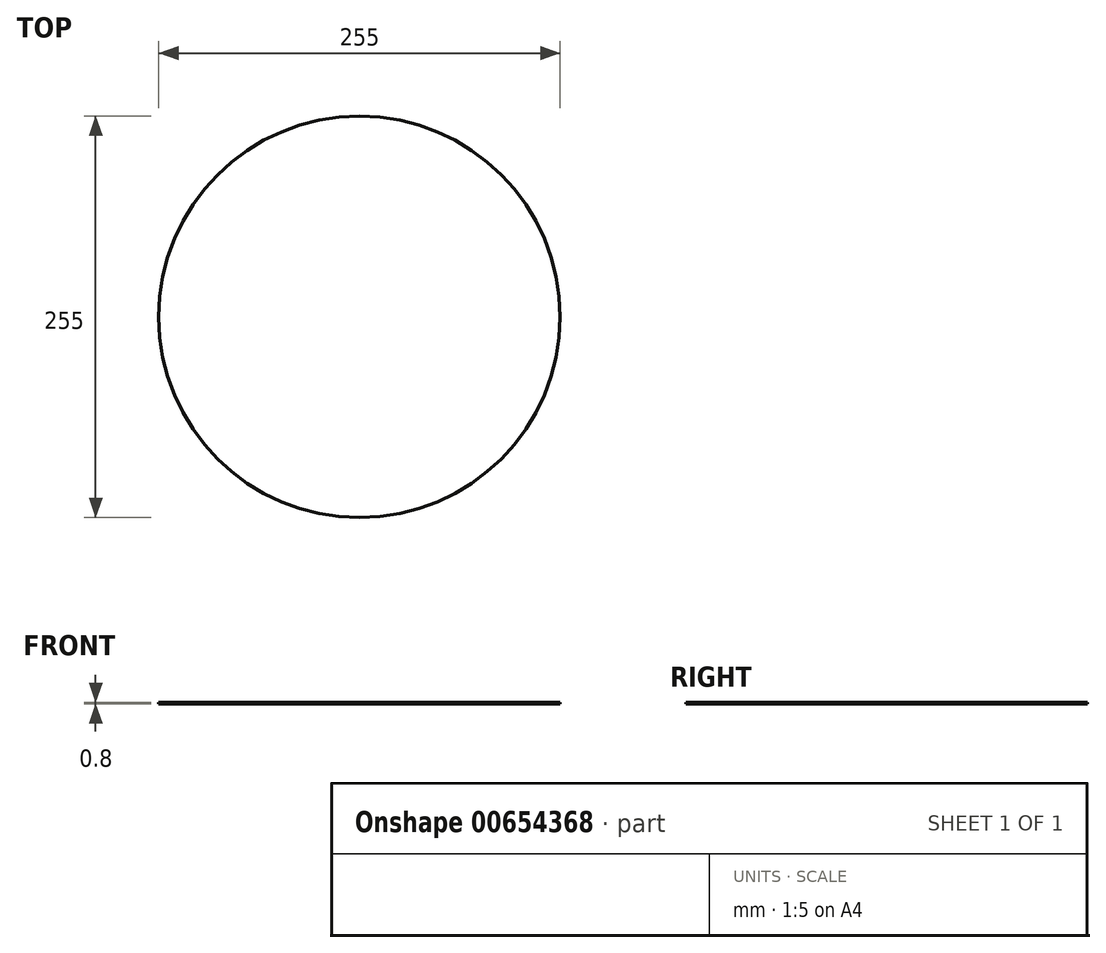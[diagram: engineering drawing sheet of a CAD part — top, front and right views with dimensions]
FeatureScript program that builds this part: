
annotation { "Feature Type Name" : "Feature", "Feature Type Description" : "" }
export const myFeature = defineFeature(function(context is Context, id is Id, definition is map)
    precondition{}
    {
        {
            var Q0;
            Q0=qCreatedBy(makeId("Top.planeOp"),FACE);
            var sketch = newSketch(context, id + "F0", { "sketchPlane" : qUnion([Q0])});
            skCircle(sketch, "E0", {"center": v(0, 0) * mm, "radius": 127.5 * mm});
            skSolve(sketch);
        }
        {
            var Q0;
            Q0 = qSketchRegion(id + "F0", true);
            extrude(context, id + "F1", {"entities" : qUnion([Q0]), "depth" : 0.8 * mm, "offsetDistance" : 25 * mm});
        }
    });
